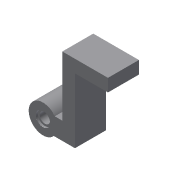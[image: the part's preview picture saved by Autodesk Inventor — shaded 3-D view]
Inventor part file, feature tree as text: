
AUTODESK INVENTOR PART (.ipt)
format: ipt  version: 2015 (Build 190159000, 159)  size: 135,168 bytes
history: native  units: in
note: dims shown in document units (in); Inventor stores cm internally (conversion verified against a paired STEP export)
features: extrude x5, sketch x5, mirror x2, reference x1, projected_geometry x1
ambient origin geometry x8: Origin, YZ Plane, XZ Plane, XY Plane, X Axis, Y Axis, Z Axis, Center Point
bodies: Solid1 (feature_tree)
feature tree (14):
  extrude  "Extrusion1"  Depth=0.9375in TaperAngle=0.0deg
  extrude  "Extrusion2"  Depth=0.4882in TaperAngle=0.0deg
  mirror  "Mirror1"
  extrude  "Extrusion3"  Depth=0.0591in TaperAngle=0.0deg
  extrude  "Extrusion4"  Depth=0.3831in
  mirror  "Mirror2"
  extrude  "Extrusion5"  [1 undecoded]
  sketch  "Sketch1"  dims[d0=0.375in d1=0.0in d2=0.9375in d3=0.0in]
  reference  "Reference1"
  sketch  "Sketch2"  dims[d4=0.3125in d5=0.4882in d6=0.0in]
  sketch  "Sketch3"  dims[d7=0.4331in d8=0.0591in d9=0.0in]
  sketch  "Sketch4"  dims[d11=2.3455in d12=0.3831in]
  sketch  "Sketch7"  dims[d13=1.0in d14=0.0in]
  projected_geometry  "Projected Loop1"
note: 1 required parameter value undecoded (feature->parameter linkage not recoverable at this tier; creation-order binding heuristic only, values carry confidence <= 0.55)
